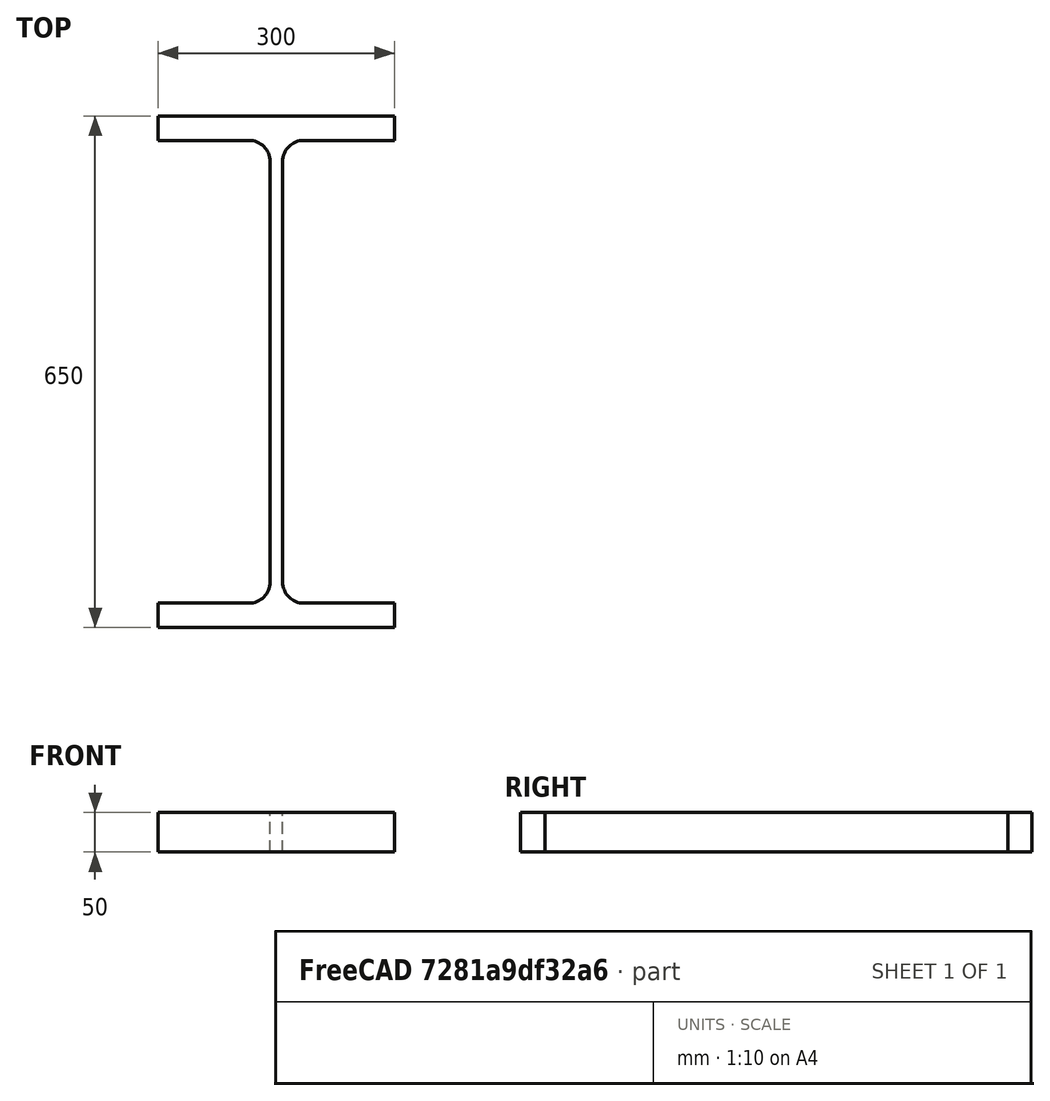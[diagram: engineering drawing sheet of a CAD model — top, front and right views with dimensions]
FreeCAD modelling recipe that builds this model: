
FCSTD DOCUMENT  (FreeCAD 0.15R4671 (Git))
Label: HE-B-Profile 650 DIN1025-2 S235JR
License: All rights reserved
LicenseURL: http://en.wikipedia.org/wiki/All_rights_reserved
objects: Sketcher::SketchObject×1, Part::Extrusion×1
note: 2 computed .brp shape members not serialized (recipe doc carries the construction recipe); baked Part::Feature solids carry a one-line shape summary decoded from their .brp

FEATURE [Sketcher::SketchObject] Sketch
  sketch-geometry (16):
    g0: LineSegment StartX=8 StartY=-267 StartZ=0 EndX=8 EndY=267 EndZ=0
    g1: LineSegment StartX=35 StartY=294 StartZ=0 EndX=150 EndY=294 EndZ=0
    g2: LineSegment StartX=150 StartY=294 StartZ=0 EndX=150 EndY=325 EndZ=0
    g3: LineSegment StartX=150 StartY=325 StartZ=0 EndX=-150 EndY=325 EndZ=0
    g4: LineSegment StartX=-150 StartY=325 StartZ=0 EndX=-150 EndY=294 EndZ=0
    g5: LineSegment StartX=-150 StartY=294 StartZ=0 EndX=-35 EndY=294 EndZ=0
    g6: LineSegment StartX=-8 StartY=267 StartZ=0 EndX=-8 EndY=-267 EndZ=0
    g7: LineSegment StartX=-35 StartY=-294 StartZ=0 EndX=-150 EndY=-294 EndZ=0
    g8: LineSegment StartX=-150 StartY=-294 StartZ=0 EndX=-150 EndY=-325 EndZ=0
    g9: LineSegment StartX=-150 StartY=-325 StartZ=0 EndX=150 EndY=-325 EndZ=0
    g10: LineSegment StartX=150 StartY=-325 StartZ=0 EndX=150 EndY=-294 EndZ=0
    g11: LineSegment StartX=150 StartY=-294 StartZ=0 EndX=35 EndY=-294 EndZ=0
    g12: ArcOfCircle CenterX=35 CenterY=267 CenterZ=0 NormalX=0 NormalY=0 NormalZ=1 Radius=27 StartAngle=1.5708 EndAngle=3.14159
    g13: ArcOfCircle CenterX=35 CenterY=-267 CenterZ=0 NormalX=0 NormalY=0 NormalZ=1 Radius=27 StartAngle=3.14159 EndAngle=4.71239
    g14: ArcOfCircle CenterX=-35 CenterY=267 CenterZ=0 NormalX=0 NormalY=0 NormalZ=1 Radius=27 StartAngle=0 EndAngle=1.5708
    g15: ArcOfCircle CenterX=-35 CenterY=-267 CenterZ=0 NormalX=0 NormalY=0 NormalZ=1 Radius=27 StartAngle=4.71239 EndAngle=6.28319
  constraints (42):
    c: Vertical(g0)
    c: Coincident(g2,g1)
    c: Vertical(g2)
    c: Coincident(g3,g2)
    c: Coincident(g4,g3)
    c: Vertical(g4)
    c: Coincident(g5,g4)
    c: Horizontal(g5)
    c: Vertical(g6)
    c: Horizontal(g7)
    c: Coincident(g8,g7)
    c: Vertical(g8)
    c: Coincident(g9,g8)
    c: Horizontal(g9)
    c: Coincident(g10,g9)
    c: Vertical(g10)
    c: Coincident(g11,g10)
    c: Horizontal(g11)
    c: Tangent(g1,g12) = 1.5708
    c: Tangent(g0,g12) = 1.5708
    c: Tangent(g0,g13) = 1.5708
    c: Tangent(g11,g13) = 1.5708
    c: Tangent(g5,g14) = 1.5708
    c: Tangent(g6,g14) = 1.5708
    c: Tangent(g6,g15) = 1.5708
    c: Tangent(g7,g15) = 1.5708
    c: Equal(g3,g9)
    c: Equal(g2,g4)
    c: Equal(g4,g8)
    c: Equal(g8,g10)
    c: Equal(g12,g14)
    c: Equal(g14,g15)
    c: Equal(g15,g13)
    c: Symmetric(g2,g3,g-2)
    c: Symmetric(g9,g8,g-2)
    c: Symmetric(g0,g6,g-2)
    c: Symmetric(g2,g9,g-1)
    c: DistanceY(g2,g9) = -650
    c: DistanceX(g3) = -300
    c: DistanceX(g0,g6) = -16
    c: DistanceY(g2) = 31
    c: Radius(g12) = 27
FEATURE [Part::Extrusion] Extrude  label="HE-B-Profile 650 DIN1025-2 S235JR"
  Base = -> Sketch
  Dir = (0,0,50)
  Solid = true
